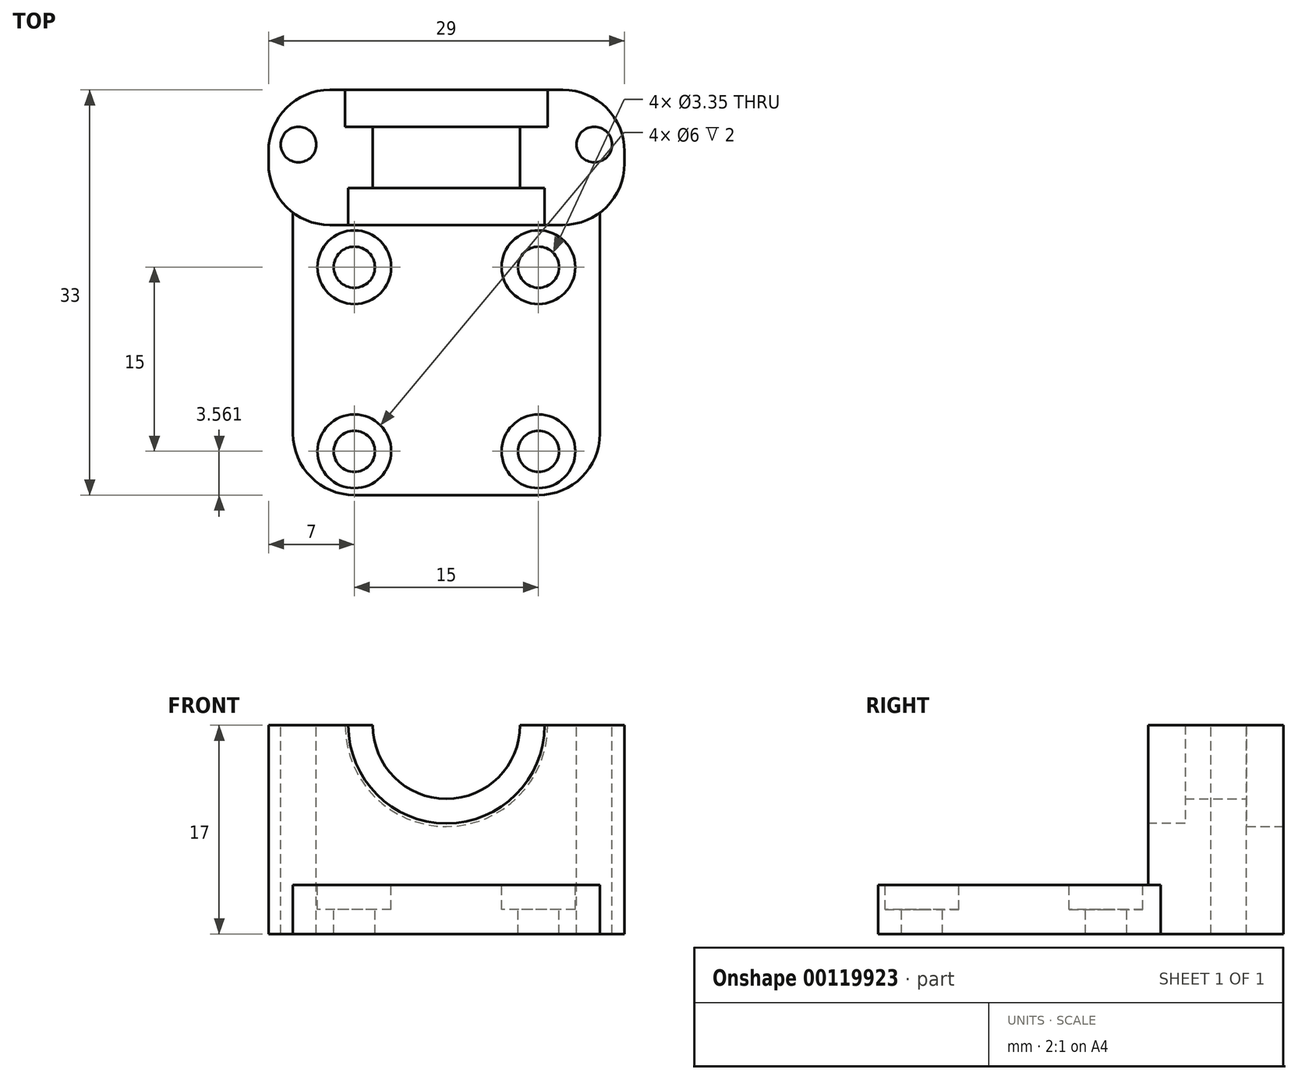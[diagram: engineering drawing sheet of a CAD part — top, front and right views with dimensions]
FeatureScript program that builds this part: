
annotation { "Feature Type Name" : "Feature", "Feature Type Description" : "" }
export const myFeature = defineFeature(function(context is Context, id is Id, definition is map)
    precondition{}
    {
        {
            var Q0;
            Q0=qCreatedBy(makeId("Top.planeOp"),FACE);
            var sketch = newSketch(context, id + "F0", { "sketchPlane" : qUnion([Q0])});
            skLineSegment(sketch, "E0.bottom", {"start": v(0, 0) * mm, "end": v(25, 0) * mm});
            skLineSegment(sketch, "E0.top", {"start": v(0, 33) * mm, "end": v(25, 33) * mm});
            skLineSegment(sketch, "E0.left", {"start": v(0, 0) * mm, "end": v(0, 33) * mm});
            skLineSegment(sketch, "E0.right", {"start": v(25, 0) * mm, "end": v(25, 33) * mm});
            skSolve(sketch);
        }
        {
            var Q0;
            Q0=qSketchRegion(id+"F0",true);
            extrude(context, id + "F1", {"entities" : qUnion([Q0]), "depth" : 4 * mm});
        }
        {
            var Q0;
            Q0=makeQuery(id+"F1.opExtrude","CAP_FACE",FACE,{"disambiguationData":[OSD([sQuery(id+"F0.wireOp",EDGE,"E0.bottom"),sQuery(id+"F0.wireOp",EDGE,"E0.top"),sQuery(id+"F0.wireOp",EDGE,"E0.left"),sQuery(id+"F0.wireOp",EDGE,"E0.right")])],"isStart":false});
            var sketch = newSketch(context, id + "F2", { "sketchPlane" : qUnion([Q0])});
            skCircle(sketch, "E1", {"center": v(5, 18.56) * mm, "radius": 1.68 * mm});
            skCircle(sketch, "E2", {"center": v(20, 18.56) * mm, "radius": 1.68 * mm});
            skCircle(sketch, "E3", {"center": v(5, 3.56) * mm, "radius": 1.68 * mm});
            skCircle(sketch, "E4", {"center": v(20, 3.56) * mm, "radius": 1.68 * mm});
            skLineSegment(sketch, "E5", {"start": v(5, 18.56) * mm, "end": v(0, 18.56) * mm});
            skLineSegment(sketch, "E6", {"start": v(20, 3.56) * mm, "end": v(25, 3.56) * mm});
            skCircle(sketch, "E7", {"center": v(5, 18.56) * mm, "radius": 3 * mm});
            skCircle(sketch, "E8", {"center": v(20, 18.56) * mm, "radius": 3 * mm});
            skCircle(sketch, "E9", {"center": v(5, 3.56) * mm, "radius": 3 * mm});
            skCircle(sketch, "E10", {"center": v(20, 3.56) * mm, "radius": 3 * mm});
            skSolve(sketch);
        }
        {
            var Q0;
            Q0=makeQuery(id+"F2.imprint","IMPRINT",FACE,{"disambiguationData":[TD([[makeQuery(id+"F2.imprint","IMPRINT",EDGE,{"derivedFrom":sQuery(id+"F2.wireOp",EDGE,"E1")}),1.0]])]});
            var Q1;
            Q1=makeQuery(id+"F2.imprint","IMPRINT",FACE,{"disambiguationData":[TD([[makeQuery(id+"F2.imprint","IMPRINT",EDGE,{"derivedFrom":sQuery(id+"F2.wireOp",EDGE,"E2")}),1.0]])]});
            var Q2;
            Q2=makeQuery(id+"F2.imprint","IMPRINT",FACE,{"disambiguationData":[TD([[makeQuery(id+"F2.imprint","IMPRINT",EDGE,{"derivedFrom":sQuery(id+"F2.wireOp",EDGE,"E4")}),1.0]])]});
            var Q3;
            Q3=makeQuery(id+"F2.imprint","IMPRINT",FACE,{"disambiguationData":[TD([[makeQuery(id+"F2.imprint","IMPRINT",EDGE,{"derivedFrom":sQuery(id+"F2.wireOp",EDGE,"E3")}),1.0]])]});
            extrude(context, id + "F3", {"entities" : qUnion([Q0, Q1, Q2, Q3]), "operationType" : NewBodyOperationType.REMOVE, "oppositeDirection" : true, "depth" : 25 * mm});
        }
        {
            var Q0;
            Q0=makeQuery(id+"F1.opExtrude","CAP_FACE",FACE,{"disambiguationData":[OSD([sQuery(id+"F0.wireOp",EDGE,"E0.bottom"),sQuery(id+"F0.wireOp",EDGE,"E0.top"),sQuery(id+"F0.wireOp",EDGE,"E0.left"),sQuery(id+"F0.wireOp",EDGE,"E0.right")])],"isStart":false});
            var sketch = newSketch(context, id + "F4", { "sketchPlane" : qUnion([Q0])});
            skLineSegment(sketch, "E11.bottom", {"start": v(0, 33) * mm, "end": v(25, 33) * mm});
            skLineSegment(sketch, "E11.top", {"start": v(0, 22) * mm, "end": v(25, 22) * mm});
            skLineSegment(sketch, "E11.left", {"start": v(0, 33) * mm, "end": v(0, 22) * mm});
            skLineSegment(sketch, "E11.right", {"start": v(25, 33) * mm, "end": v(25, 22) * mm});
            skSolve(sketch);
        }
        {
            var Q0;
            Q0=qSketchRegion(id+"F4",true);
            extrude(context, id + "F5", {"entities" : qUnion([Q0]), "operationType" : NewBodyOperationType.ADD, "depth" : 13 * mm});
        }
        {
            var Q0;
            Q0=makeQuery(id+"F5.boolean.opBoolean","MERGE",FACE,{"derivedFrom":[makeQuery(id+"F1.opExtrude","SWEPT_FACE",FACE,{"disambiguationData":[OSD([sQuery(id+"F0.wireOp",EDGE,"E0.top")])]}),makeQuery(id+"F5.opExtrude","SWEPT_FACE",FACE,{"disambiguationData":[OSD([sQuery(id+"F4.wireOp",EDGE,"E11.bottom")])]})]});
            var sketch = newSketch(context, id + "F6", { "sketchPlane" : qUnion([Q0])});
            skCircle(sketch, "E12", {"center": v(-12.5, 17) * mm, "radius": 6 * mm});
            skSolve(sketch);
        }
        {
            var Q0;
            {var subQ0=makeQuery(id+"F5.opExtrude","CAP_EDGE",EDGE,{"disambiguationData":[OSD([sQuery(id+"F4.wireOp",EDGE,"E11.bottom")])],"isStart":false});var subQ1=sQuery(id+"F6.wireOp",EDGE,"E12");var subQ3=makeQuery(id+"F6.imprint","INTERSECT",VERTEX,{"disambiguationData":[OD(0.0)],"derivedFrom":[subQ0,subQ1]});Q0=makeQuery(id+"F6.imprint","IMPRINT",FACE,{"disambiguationData":[TD([[makeQuery(id+"F6.imprint","IMPRINT",EDGE,{"disambiguationData":[TD([[subQ3,1.0]])],"derivedFrom":subQ1}),1.0]])]});}
            extrude(context, id + "F7", {"entities" : qUnion([Q0]), "operationType" : NewBodyOperationType.REMOVE, "oppositeDirection" : true, "depth" : 9 * mm});
        }
        {
            var Q0;
            Q0=makeQuery(id+"F5.opExtrude","SWEPT_FACE",FACE,{"disambiguationData":[OSD([sQuery(id+"F4.wireOp",EDGE,"E11.top")])]});
            var sketch = newSketch(context, id + "F8", { "sketchPlane" : qUnion([Q0])});
            skCircle(sketch, "E13", {"center": v(12.5, 17) * mm, "radius": 8 * mm});
            skSolve(sketch);
        }
        {
            var Q0;
            Q0=qSketchRegion(id+"F8",true);
            extrude(context, id + "F9", {"entities" : qUnion([Q0]), "operationType" : NewBodyOperationType.REMOVE, "oppositeDirection" : true, "depth" : 3 * mm});
        }
        {
            var Q0;
            Q0=makeQuery(id+"F2.imprint","IMPRINT",FACE,{"disambiguationData":[TD([[makeQuery(id+"F2.imprint","IMPRINT",EDGE,{"derivedFrom":sQuery(id+"F2.wireOp",EDGE,"E1")}),-1.0]])]});
            var Q1;
            Q1=makeQuery(id+"F2.imprint","IMPRINT",FACE,{"disambiguationData":[TD([[makeQuery(id+"F2.imprint","IMPRINT",EDGE,{"derivedFrom":sQuery(id+"F2.wireOp",EDGE,"E2")}),-1.0]])]});
            var Q2;
            Q2=makeQuery(id+"F2.imprint","IMPRINT",FACE,{"disambiguationData":[TD([[makeQuery(id+"F2.imprint","IMPRINT",EDGE,{"derivedFrom":sQuery(id+"F2.wireOp",EDGE,"E4")}),-1.0]])]});
            var Q3;
            Q3=makeQuery(id+"F2.imprint","IMPRINT",FACE,{"disambiguationData":[TD([[makeQuery(id+"F2.imprint","IMPRINT",EDGE,{"derivedFrom":sQuery(id+"F2.wireOp",EDGE,"E3")}),-1.0]])]});
            extrude(context, id + "F10", {"entities" : qUnion([Q0, Q1, Q2, Q3]), "operationType" : NewBodyOperationType.REMOVE, "oppositeDirection" : true, "depth" : 2 * mm});
        }
        {
            var Q0;
            Q0=makeQuery(id+"F1.opExtrude","SWEPT_EDGE",EDGE,{"disambiguationData":[OSD([sQuery(id+"F0.wireOp",EDGE,"E0.bottom"),sQuery(id+"F0.wireOp",EDGE,"E0.left")])]});
            var Q1;
            Q1=makeQuery(id+"F1.opExtrude","SWEPT_EDGE",EDGE,{"disambiguationData":[OSD([sQuery(id+"F0.wireOp",EDGE,"E0.bottom"),sQuery(id+"F0.wireOp",EDGE,"E0.right")])]});
            fillet(context, id + "F11", {"entities" : qUnion([Q0, Q1]), "radius" : 5 * mm, "tangentPropagation" : true, "allowEdgeOverflow" : false});
        }
        {
            var Q0;
            Q0=makeQuery(id+"F5.boolean.opBoolean","MERGE",FACE,{"derivedFrom":[makeQuery(id+"F1.opExtrude","SWEPT_FACE",FACE,{"disambiguationData":[OSD([sQuery(id+"F0.wireOp",EDGE,"E0.left")])]}),makeQuery(id+"F5.opExtrude","SWEPT_FACE",FACE,{"disambiguationData":[OSD([sQuery(id+"F4.wireOp",EDGE,"E11.left")])]})]});
            var sketch = newSketch(context, id + "F12", { "sketchPlane" : qUnion([Q0])});
            skLineSegment(sketch, "E14.bottom", {"start": v(-33, 0) * mm, "end": v(-22, 0) * mm});
            skLineSegment(sketch, "E14.top", {"start": v(-33, 17) * mm, "end": v(-22, 17) * mm});
            skLineSegment(sketch, "E14.left", {"start": v(-33, 0) * mm, "end": v(-33, 17) * mm});
            skLineSegment(sketch, "E14.right", {"start": v(-22, 0) * mm, "end": v(-22, 17) * mm});
            skSolve(sketch);
        }
        {
            var Q0;
            Q0=qSketchRegion(id+"F12",true);
            extrude(context, id + "F13", {"entities" : qUnion([Q0]), "operationType" : NewBodyOperationType.ADD, "depth" : 2 * mm});
        }
        {
            var Q0;
            Q0=makeQuery(id+"F5.boolean.opBoolean","MERGE",FACE,{"derivedFrom":[makeQuery(id+"F1.opExtrude","SWEPT_FACE",FACE,{"disambiguationData":[OSD([sQuery(id+"F0.wireOp",EDGE,"E0.right")])]}),makeQuery(id+"F5.opExtrude","SWEPT_FACE",FACE,{"disambiguationData":[OSD([sQuery(id+"F4.wireOp",EDGE,"E11.right")])]})]});
            var sketch = newSketch(context, id + "F14", { "sketchPlane" : qUnion([Q0])});
            skLineSegment(sketch, "E15.bottom", {"start": v(33, 0) * mm, "end": v(22, 0) * mm});
            skLineSegment(sketch, "E15.top", {"start": v(33, 17) * mm, "end": v(22, 17) * mm});
            skLineSegment(sketch, "E15.left", {"start": v(33, 0) * mm, "end": v(33, 17) * mm});
            skLineSegment(sketch, "E15.right", {"start": v(22, 0) * mm, "end": v(22, 17) * mm});
            skSolve(sketch);
        }
        {
            var Q0;
            Q0=qSketchRegion(id+"F14",true);
            extrude(context, id + "F15", {"entities" : qUnion([Q0]), "operationType" : NewBodyOperationType.ADD, "depth" : 2 * mm});
        }
        {
            var Q0;
            {var subQ0=sQuery(id+"F4.wireOp",EDGE,"E11.bottom");var subQ1=sQuery(id+"F4.wireOp",EDGE,"E11.top");var subQ2=sQuery(id+"F4.wireOp",EDGE,"E11.left");Q0=makeQuery(id+"F9.boolean.opBoolean","SPLIT",FACE,{"disambiguationData":[TD([makeQuery(id+"F1.opExtrude","SWEPT_FACE",FACE,{"disambiguationData":[OSD([sQuery(id+"F0.wireOp",EDGE,"E0.left")])]})])],"derivedFrom":makeQuery(id+"F5.opExtrude","CAP_FACE",FACE,{"disambiguationData":[OSD([subQ0,subQ1,subQ2,sQuery(id+"F4.wireOp",EDGE,"E11.right")])],"isStart":false})});}
            var sketch = newSketch(context, id + "F16", { "sketchPlane" : qUnion([Q0])});
            skCircle(sketch, "E16", {"center": v(0.45, 28.55) * mm, "radius": 1.45 * mm});
            skCircle(sketch, "E17", {"center": v(24.55, 28.55) * mm, "radius": 1.45 * mm});
            skSolve(sketch);
        }
        {
            var Q0;
            Q0=qSketchRegion(id+"F16",true);
            extrude(context, id + "F17", {"entities" : qUnion([Q0]), "operationType" : NewBodyOperationType.REMOVE, "oppositeDirection" : true, "depth" : 25 * mm});
        }
        {
            var Q0;
            Q0=makeQuery(id+"F13.opExtrude","CAP_EDGE",EDGE,{"disambiguationData":[OSD([sQuery(id+"F12.wireOp",EDGE,"E14.right")])],"isStart":false});
            var Q1;
            Q1=makeQuery(id+"F13.opExtrude","CAP_EDGE",EDGE,{"disambiguationData":[OSD([sQuery(id+"F12.wireOp",EDGE,"E14.left")])],"isStart":false});
            var Q2;
            Q2=makeQuery(id+"F15.opExtrude","CAP_EDGE",EDGE,{"disambiguationData":[OSD([sQuery(id+"F14.wireOp",EDGE,"E15.left")])],"isStart":false});
            var Q3;
            Q3=makeQuery(id+"F15.opExtrude","CAP_EDGE",EDGE,{"disambiguationData":[OSD([sQuery(id+"F14.wireOp",EDGE,"E15.right")])],"isStart":false});
            fillet(context, id + "F18", {"entities" : qUnion([Q0, Q1, Q2, Q3]), "radius" : 5 * mm, "tangentPropagation" : true, "allowEdgeOverflow" : false});
        }
        {
            var Q0;
            Q0=makeQuery(id+"F15.boolean.opBoolean","MERGE",FACE,{"derivedFrom":[makeQuery(id+"F13.boolean.opBoolean","MERGE",FACE,{"derivedFrom":[makeQuery(id+"F5.boolean.opBoolean","MERGE",FACE,{"derivedFrom":[makeQuery(id+"F1.opExtrude","SWEPT_FACE",FACE,{"disambiguationData":[OSD([sQuery(id+"F0.wireOp",EDGE,"E0.top")])]}),makeQuery(id+"F5.opExtrude","SWEPT_FACE",FACE,{"disambiguationData":[OSD([sQuery(id+"F4.wireOp",EDGE,"E11.bottom")])]})]}),makeQuery(id+"F13.opExtrude","SWEPT_FACE",FACE,{"disambiguationData":[OSD([sQuery(id+"F12.wireOp",EDGE,"E14.left")])]})]}),makeQuery(id+"F15.opExtrude","SWEPT_FACE",FACE,{"disambiguationData":[OSD([sQuery(id+"F14.wireOp",EDGE,"E15.left")])]})]});
            var sketch = newSketch(context, id + "F19", { "sketchPlane" : qUnion([Q0])});
            skCircle(sketch, "E18", {"center": v(-12.5, 17) * mm, "radius": 8.25 * mm});
            skSolve(sketch);
        }
        {
            var Q0;
            Q0=qSketchRegion(id+"F19",true);
            extrude(context, id + "F20", {"entities" : qUnion([Q0]), "operationType" : NewBodyOperationType.REMOVE, "oppositeDirection" : true, "depth" : 3 * mm});
        }
    });
